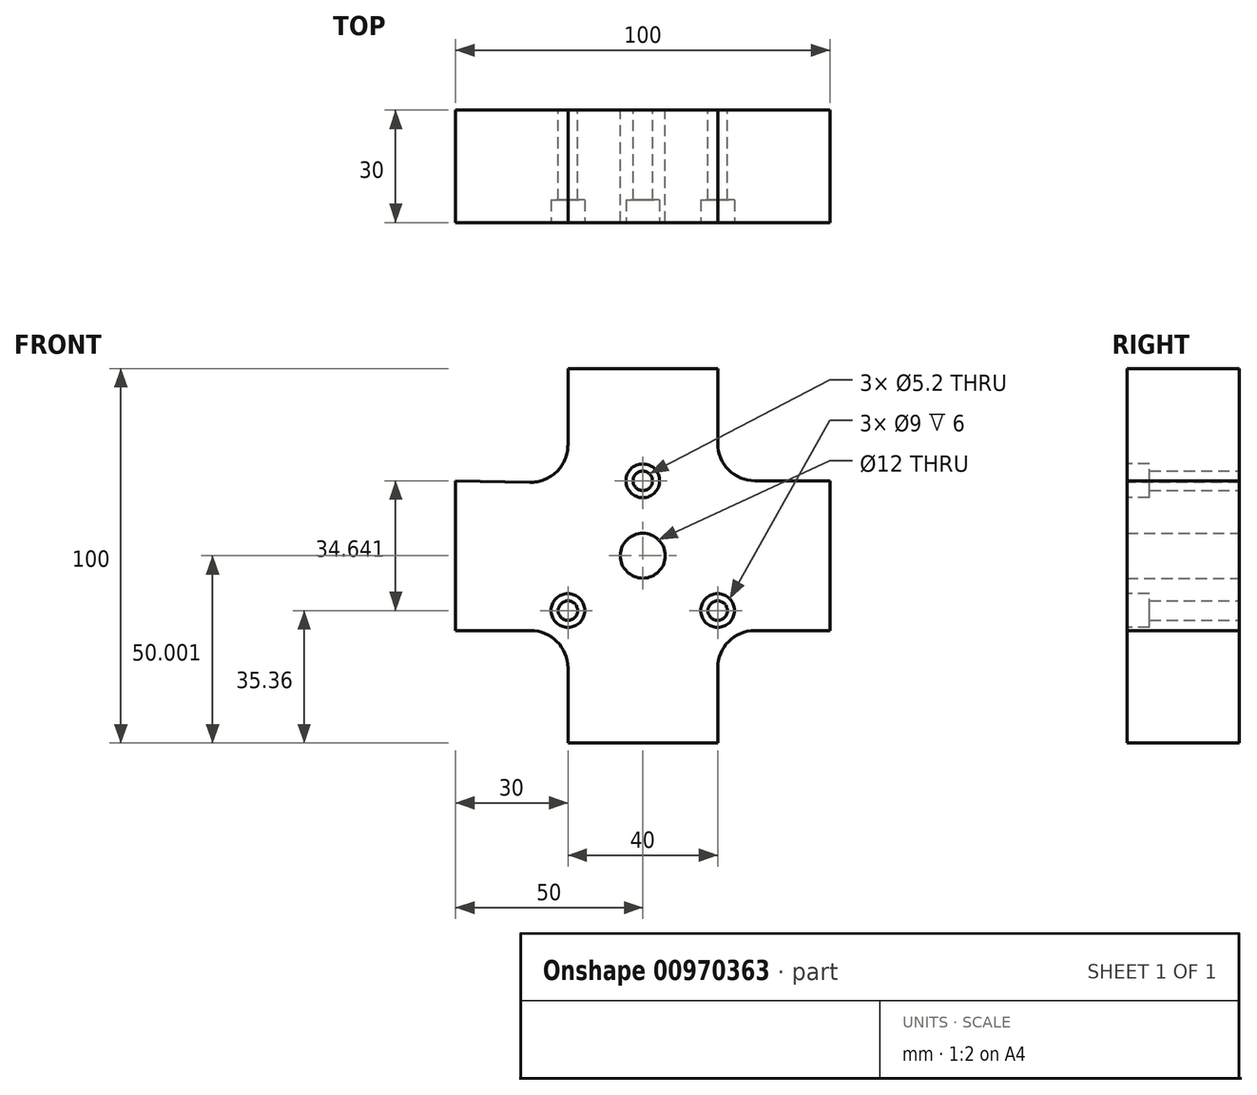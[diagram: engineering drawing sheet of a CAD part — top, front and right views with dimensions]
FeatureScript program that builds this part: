
annotation { "Feature Type Name" : "Feature", "Feature Type Description" : "" }
export const myFeature = defineFeature(function(context is Context, id is Id, definition is map)
    precondition{}
    {
        {
            var Q0;
            Q0=qCreatedBy(makeId("Front.planeOp"),FACE);
            var sketch = newSketch(context, id + "F0", { "sketchPlane" : qUnion([Q0])});
            skLineSegment(sketch, "E0", {"start": v(0, 0) * mm, "end": v(-20, 0) * mm, "construction": true});
            skLineSegment(sketch, "E1", {"start": v(0, 0) * mm, "end": v(20, 0) * mm, "construction": true});
            skLineSegment(sketch, "E2", {"start": v(-20, 0) * mm, "end": v(0, 34.64) * mm, "construction": true});
            skLineSegment(sketch, "E3", {"start": v(0, 34.64) * mm, "end": v(20, 0) * mm, "construction": true});
            skCircle(sketch, "E4", {"center": v(0, 34.64) * mm, "radius": 2.6 * mm});
            skCircle(sketch, "E5", {"center": v(-20, 0) * mm, "radius": 2.6 * mm});
            skCircle(sketch, "E6", {"center": v(20, 0) * mm, "radius": 2.6 * mm});
            skLineSegment(sketch, "E7", {"start": v(-20, 0) * mm, "end": v(-10, 17.32) * mm, "construction": true});
            skLineSegment(sketch, "E8", {"start": v(-10, 17.32) * mm, "end": v(20, 0) * mm, "construction": true});
            skLineSegment(sketch, "E9", {"start": v(10, 17.32) * mm, "end": v(-20, 0) * mm, "construction": true});
            skLineSegment(sketch, "E10", {"start": v(0, 0) * mm, "end": v(0, 11.55) * mm, "construction": true});
            skLineSegment(sketch, "E11", {"start": v(-10, 17.32) * mm, "end": v(10, 17.32) * mm, "construction": true});
            skLineSegment(sketch, "E12", {"start": v(0, 14.64) * mm, "end": v(37.53, 14.64) * mm, "construction": true});
            skCircle(sketch, "E13", {"center": v(0, 14.64) * mm, "radius": 6 * mm});
            skSolve(sketch);
        }
        {
            var Q0;
            Q0=qCreatedBy(makeId("Front.planeOp"),FACE);
            var sketch = newSketch(context, id + "F1", { "sketchPlane" : qUnion([Q0])});
            skLineSegment(sketch, "E14.0", {"start": v(0, 14.64) * mm, "end": v(37.53, 14.64) * mm});
            skLineSegment(sketch, "E15.bottom", {"start": v(-50, -35.36) * mm, "end": v(50, -35.36) * mm});
            skLineSegment(sketch, "E15.top", {"start": v(-50, 64.64) * mm, "end": v(50, 64.64) * mm});
            skLineSegment(sketch, "E15.left", {"start": v(-50, -35.36) * mm, "end": v(-50, 64.64) * mm});
            skLineSegment(sketch, "E15.right", {"start": v(50, -35.36) * mm, "end": v(50, 64.64) * mm});
            skPoint(sketch, "E15.middle", {"position": v(0, 14.64) * mm});
            skLineSegment(sketch, "E16.left", {"start": v(88.6, 24.64) * mm, "end": v(88.6, 4.64) * mm});
            skLineSegment(sketch, "E16.right", {"start": v(11.4, 24.64) * mm, "end": v(11.4, 4.64) * mm});
            skPoint(sketch, "E16.middle", {"position": v(50, 14.64) * mm});
            skLineSegment(sketch, "E17", {"start": v(88.6, 24.64) * mm, "end": v(50, 24.64) * mm});
            skLineSegment(sketch, "E18", {"start": v(88.6, 4.64) * mm, "end": v(50, 4.64) * mm});
            skLineSegment(sketch, "E19.MirrorCS", {"start": v(-88.6, 24.64) * mm, "end": v(-88.6, 4.64) * mm});
            skLineSegment(sketch, "E20.MirrorCS", {"start": v(-88.6, 24.64) * mm, "end": v(-50, 24.64) * mm});
            skLineSegment(sketch, "E21.MirrorCS", {"start": v(-88.6, 4.64) * mm, "end": v(-50, 4.64) * mm});
            skSolve(sketch);
        }
        {
            var Q0;
            Q0=makeQuery(id+"F1.imprint","IMPRINT",FACE,{"disambiguationData":[TD([[makeQuery(id+"F1.imprint","IMPRINT",EDGE,{"derivedFrom":sQuery(id+"F1.wireOp",EDGE,"E15.bottom")}),1.0]])]});
            extrude(context, id + "F2", {"entities" : qUnion([Q0]), "depth" : 30 * mm, "offsetDistance" : 25 * mm});
        }
        {
            var Q0;
            Q0 = qSketchRegion(id + "F0", true);
            extrude(context, id + "F3", {"entities" : qUnion([Q0]), "operationType" : NewBodyOperationType.REMOVE, "depth" : 50 * mm, "offsetDistance" : 25 * mm});
        }
        {
            var Q0;
            Q0=makeQuery(id+"F2.opExtrude","CAP_FACE",FACE,{"disambiguationData":[OSD([sQuery(id+"F1.wireOp",EDGE,"E15.bottom"),sQuery(id+"F1.wireOp",EDGE,"E15.top"),sQuery(id+"F1.wireOp",EDGE,"E15.left"),sQuery(id+"F1.wireOp",EDGE,"E15.right")])],"isStart":false});
            var sketch = newSketch(context, id + "F4", { "sketchPlane" : qUnion([Q0])});
            skCircle(sketch, "E22.0", {"center": v(0, 34.64) * mm, "radius": 4.5 * mm});
            skCircle(sketch, "E23.0", {"center": v(20, 0) * mm, "radius": 4.5 * mm});
            skCircle(sketch, "E24.0", {"center": v(-20, 0) * mm, "radius": 4.5 * mm});
            skSolve(sketch);
        }
        {
            var Q0;
            Q0 = qSketchRegion(id + "F4", true);
            extrude(context, id + "F5", {"entities" : qUnion([Q0]), "operationType" : NewBodyOperationType.REMOVE, "oppositeDirection" : true, "depth" : 6 * mm, "offsetDistance" : 25 * mm});
        }
        {
            var Q0;
            Q0=makeQuery(id+"F2.opExtrude","CAP_FACE",FACE,{"disambiguationData":[OSD([sQuery(id+"F1.wireOp",EDGE,"E15.bottom"),sQuery(id+"F1.wireOp",EDGE,"E15.top"),sQuery(id+"F1.wireOp",EDGE,"E15.left"),sQuery(id+"F1.wireOp",EDGE,"E15.right")])],"isStart":true});
            var sketch = newSketch(context, id + "F6", { "sketchPlane" : qUnion([Q0])});
            skLineSegment(sketch, "E25", {"start": v(-50, 64.64) * mm, "end": v(-20, 64.64) * mm, "construction": true});
            skLineSegment(sketch, "E26", {"start": v(-50, 64.64) * mm, "end": v(-20, 64.64) * mm});
            skLineSegment(sketch, "E27", {"start": v(-20, 34.64) * mm, "end": v(-20, 64.64) * mm});
            skLineSegment(sketch, "E28", {"start": v(-20, 34.64) * mm, "end": v(-50, 34.64) * mm});
            skLineSegment(sketch, "E29", {"start": v(-50, 34.64) * mm, "end": v(-50, 64.64) * mm});
            skLineSegment(sketch, "E30", {"start": v(-50, 34.64) * mm, "end": v(-50, -35.36) * mm, "construction": true});
            skLineSegment(sketch, "E31", {"start": v(-50, -35.36) * mm, "end": v(50, -35.36) * mm, "construction": true});
            skLineSegment(sketch, "E32", {"start": v(50, -35.36) * mm, "end": v(50, 64.64) * mm, "construction": true});
            skLineSegment(sketch, "E33", {"start": v(-50, -35.36) * mm, "end": v(-50, -5.36) * mm});
            skLineSegment(sketch, "E34", {"start": v(-50, -5.36) * mm, "end": v(-20, -5.36) * mm});
            skLineSegment(sketch, "E35", {"start": v(-20, -5.36) * mm, "end": v(-20, -35.36) * mm});
            skLineSegment(sketch, "E36", {"start": v(-20, -35.36) * mm, "end": v(-50, -35.36) * mm});
            skLineSegment(sketch, "E37", {"start": v(50, -35.36) * mm, "end": v(20, -35.36) * mm});
            skLineSegment(sketch, "E38", {"start": v(20, -35.36) * mm, "end": v(20, -5.36) * mm});
            skLineSegment(sketch, "E39", {"start": v(20, -5.36) * mm, "end": v(50, -5.36) * mm});
            skLineSegment(sketch, "E40", {"start": v(50, -5.36) * mm, "end": v(50, -35.36) * mm});
            skLineSegment(sketch, "E41", {"start": v(50, 64.64) * mm, "end": v(50, 34.64) * mm});
            skLineSegment(sketch, "E42", {"start": v(50, 34.64) * mm, "end": v(20, 34.03) * mm});
            skLineSegment(sketch, "E43", {"start": v(20, 34.03) * mm, "end": v(20, 64.64) * mm});
            skLineSegment(sketch, "E44", {"start": v(20, 64.64) * mm, "end": v(50, 64.64) * mm});
            skSolve(sketch);
        }
        {
            var Q0;
            Q0=makeQuery(id+"F6.imprint","IMPRINT",FACE,{"disambiguationData":[TD([[makeQuery(id+"F6.imprint","IMPRINT",EDGE,{"derivedFrom":sQuery(id+"F6.wireOp",EDGE,"E26")}),1.0]])]});
            var Q1;
            Q1=makeQuery(id+"F6.imprint","IMPRINT",FACE,{"disambiguationData":[TD([[makeQuery(id+"F6.imprint","IMPRINT",EDGE,{"derivedFrom":sQuery(id+"F6.wireOp",EDGE,"E33")}),-1.0]])]});
            var Q2;
            Q2=makeQuery(id+"F6.imprint","IMPRINT",FACE,{"disambiguationData":[TD([[makeQuery(id+"F6.imprint","IMPRINT",EDGE,{"derivedFrom":sQuery(id+"F6.wireOp",EDGE,"E37")}),-1.0]])]});
            var Q3;
            Q3=makeQuery(id+"F6.imprint","IMPRINT",FACE,{"disambiguationData":[TD([[makeQuery(id+"F6.imprint","IMPRINT",EDGE,{"derivedFrom":sQuery(id+"F6.wireOp",EDGE,"E41")}),1.0]])]});
            extrude(context, id + "F7", {"entities" : qUnion([Q0, Q1, Q2, Q3]), "operationType" : NewBodyOperationType.REMOVE, "oppositeDirection" : true, "depth" : 50 * mm, "offsetDistance" : 25 * mm});
        }
        {
            var Q0;
            Q0=makeQuery(id+"F7.boolean.opBoolean","COPY",EDGE,{"derivedFrom":makeQuery(id+"F7.opExtrude","SWEPT_EDGE",EDGE,{"disambiguationData":[OSD([sQuery(id+"F1.wireOp",EDGE,"E15.top"),sQuery(id+"F6.wireOp",EDGE,"E43"),sQuery(id+"F6.wireOp",EDGE,"E44")])]})});
            var Q1;
            Q1=makeQuery(id+"F7.boolean.opBoolean","COPY",EDGE,{"derivedFrom":makeQuery(id+"F7.opExtrude","SWEPT_EDGE",EDGE,{"disambiguationData":[OSD([sQuery(id+"F6.wireOp",EDGE,"E42"),sQuery(id+"F6.wireOp",EDGE,"E43")])]})});
            var Q2;
            Q2=makeQuery(id+"F7.boolean.opBoolean","COPY",EDGE,{"derivedFrom":makeQuery(id+"F7.opExtrude","SWEPT_EDGE",EDGE,{"disambiguationData":[OSD([sQuery(id+"F1.wireOp",EDGE,"E15.left"),sQuery(id+"F6.wireOp",EDGE,"E41"),sQuery(id+"F6.wireOp",EDGE,"E42")])]})});
            var Q3;
            Q3=makeQuery(id+"F7.boolean.opBoolean","COPY",EDGE,{"derivedFrom":makeQuery(id+"F7.opExtrude","SWEPT_EDGE",EDGE,{"disambiguationData":[OSD([sQuery(id+"F1.wireOp",EDGE,"E15.left"),sQuery(id+"F6.wireOp",EDGE,"E39"),sQuery(id+"F6.wireOp",EDGE,"E40")])]})});
            var Q4;
            Q4=makeQuery(id+"F7.boolean.opBoolean","COPY",EDGE,{"derivedFrom":makeQuery(id+"F7.opExtrude","SWEPT_EDGE",EDGE,{"disambiguationData":[OSD([sQuery(id+"F6.wireOp",EDGE,"E38"),sQuery(id+"F6.wireOp",EDGE,"E39")])]})});
            var Q5;
            Q5=makeQuery(id+"F7.boolean.opBoolean","COPY",EDGE,{"derivedFrom":makeQuery(id+"F7.opExtrude","SWEPT_EDGE",EDGE,{"disambiguationData":[OSD([sQuery(id+"F1.wireOp",EDGE,"E15.bottom"),sQuery(id+"F6.wireOp",EDGE,"E37"),sQuery(id+"F6.wireOp",EDGE,"E38")])]})});
            var Q6;
            Q6=makeQuery(id+"F7.boolean.opBoolean","COPY",EDGE,{"derivedFrom":makeQuery(id+"F7.opExtrude","SWEPT_EDGE",EDGE,{"disambiguationData":[OSD([sQuery(id+"F1.wireOp",EDGE,"E15.bottom"),sQuery(id+"F6.wireOp",EDGE,"E35"),sQuery(id+"F6.wireOp",EDGE,"E36")])]})});
            var Q7;
            Q7=makeQuery(id+"F7.boolean.opBoolean","COPY",EDGE,{"derivedFrom":makeQuery(id+"F7.opExtrude","SWEPT_EDGE",EDGE,{"disambiguationData":[OSD([sQuery(id+"F6.wireOp",EDGE,"E34"),sQuery(id+"F6.wireOp",EDGE,"E35")])]})});
            var Q8;
            Q8=makeQuery(id+"F7.boolean.opBoolean","COPY",EDGE,{"derivedFrom":makeQuery(id+"F7.opExtrude","SWEPT_EDGE",EDGE,{"disambiguationData":[OSD([sQuery(id+"F1.wireOp",EDGE,"E15.right"),sQuery(id+"F6.wireOp",EDGE,"E33"),sQuery(id+"F6.wireOp",EDGE,"E34")])]})});
            var Q9;
            Q9=makeQuery(id+"F7.boolean.opBoolean","COPY",EDGE,{"derivedFrom":makeQuery(id+"F7.opExtrude","SWEPT_EDGE",EDGE,{"disambiguationData":[OSD([sQuery(id+"F1.wireOp",EDGE,"E15.top"),sQuery(id+"F6.wireOp",EDGE,"E26"),sQuery(id+"F6.wireOp",EDGE,"E27")])]})});
            var Q10;
            Q10=makeQuery(id+"F7.boolean.opBoolean","COPY",EDGE,{"derivedFrom":makeQuery(id+"F7.opExtrude","SWEPT_EDGE",EDGE,{"disambiguationData":[OSD([sQuery(id+"F6.wireOp",EDGE,"E27"),sQuery(id+"F6.wireOp",EDGE,"E28")])]})});
            var Q11;
            Q11=makeQuery(id+"F7.boolean.opBoolean","COPY",EDGE,{"derivedFrom":makeQuery(id+"F7.opExtrude","SWEPT_EDGE",EDGE,{"disambiguationData":[OSD([sQuery(id+"F1.wireOp",EDGE,"E15.right"),sQuery(id+"F6.wireOp",EDGE,"E28"),sQuery(id+"F6.wireOp",EDGE,"E29")])]})});
            fillet(context, id + "F8", {"entities" : qUnion([Q0, Q1, Q2, Q3, Q4, Q5, Q6, Q7, Q8, Q9, Q10, Q11]), "radius" : 10 * mm, "tangentPropagation" : true, "allowEdgeOverflow" : false});
        }
    });
